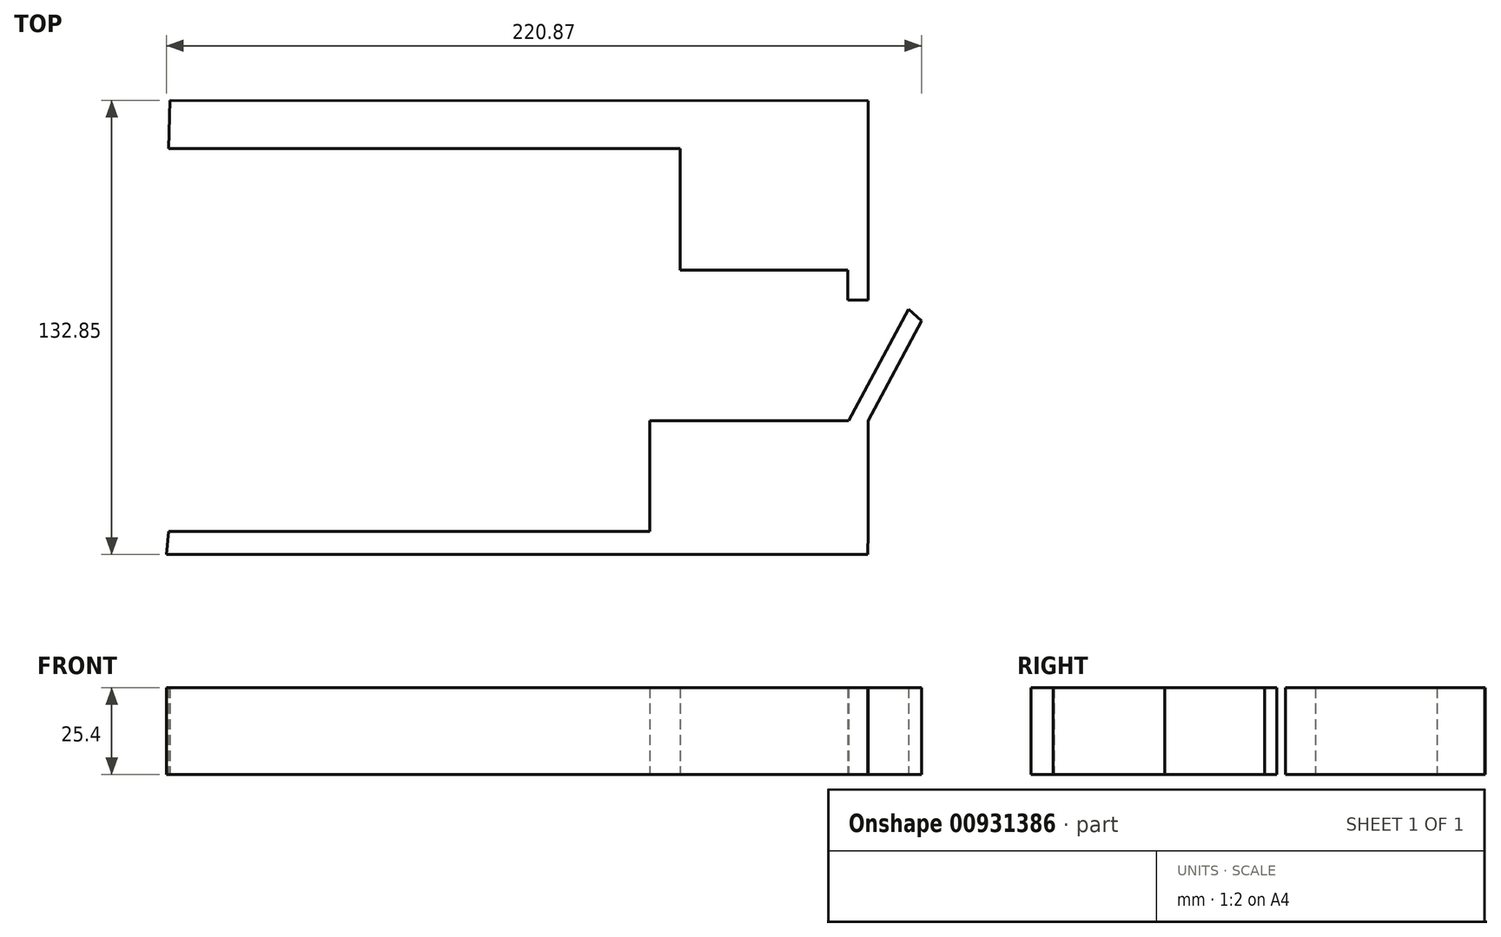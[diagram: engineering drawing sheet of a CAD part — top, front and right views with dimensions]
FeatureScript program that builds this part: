
annotation { "Feature Type Name" : "Feature", "Feature Type Description" : "" }
export const myFeature = defineFeature(function(context is Context, id is Id, definition is map)
    precondition{}
    {
        {
            var Q0;
            Q0=qCreatedBy(makeId("Top.planeOp"),FACE);
            var sketch = newSketch(context, id + "F0", { "sketchPlane" : qUnion([Q0])});
            skLineSegment(sketch, "E0", {"start": v(76.23, 56.13) * mm, "end": v(76.23, 11.87) * mm});
            skLineSegment(sketch, "E1", {"start": v(76.52, -55.86) * mm, "end": v(76.52, -23.48) * mm});
            skLineSegment(sketch, "E2", {"start": v(76.52, -23.48) * mm, "end": v(82.18, -23.48) * mm});
            skLineSegment(sketch, "E3", {"start": v(82.18, -23.48) * mm, "end": v(82.18, -56.13) * mm});
            skLineSegment(sketch, "E4", {"start": v(76.52, -55.86) * mm, "end": v(82.18, -56.13) * mm});
            skLineSegment(sketch, "E5", {"start": v(76.23, 11.87) * mm, "end": v(82.18, 11.87) * mm});
            skLineSegment(sketch, "E6", {"start": v(76.23, 56.13) * mm, "end": v(82.22, 56.13) * mm});
            skLineSegment(sketch, "E7", {"start": v(82.22, 56.13) * mm, "end": v(82.18, 11.87) * mm});
            skPoint(sketch, "E8.start.orphan", {"position": v(55.74, 0) * mm});
            skLineSegment(sketch, "E9", {"start": v(82.18, -23.48) * mm, "end": v(97.87, 5.76) * mm});
            skLineSegment(sketch, "E10", {"start": v(76.52, -23.48) * mm, "end": v(94.06, 9.22) * mm});
            skLineSegment(sketch, "E11", {"start": v(94.06, 9.22) * mm, "end": v(97.87, 5.76) * mm});
            skLineSegment(sketch, "E12", {"start": v(76.23, 56.13) * mm, "end": v(-122.33, 56.13) * mm});
            skLineSegment(sketch, "E13", {"start": v(76.52, -55.86) * mm, "end": v(-122.33, -55.86) * mm});
            skLineSegment(sketch, "E14", {"start": v(-122.33, 56.13) * mm, "end": v(-122.33, -55.86) * mm});
            skLineSegment(sketch, "E15", {"start": v(27.27, 11.87) * mm, "end": v(27.27, 56.13) * mm});
            skLineSegment(sketch, "E16", {"start": v(27.27, -38.5) * mm, "end": v(27.27, -55.86) * mm});
            skLineSegment(sketch, "E17", {"start": v(27.27, 20.64) * mm, "end": v(76.23, 20.64) * mm});
            skLineSegment(sketch, "E18", {"start": v(27.27, 50.41) * mm, "end": v(76.23, 50.41) * mm});
            skLineSegment(sketch, "E19", {"start": v(27.27, -23.48) * mm, "end": v(76.52, -23.48) * mm});
            skLineSegment(sketch, "E20", {"start": v(27.27, -23.48) * mm, "end": v(27.27, -55.86) * mm});
            skPoint(sketch, "E21.start.orphan", {"position": v(-26.78, -55.86) * mm});
            skLineSegment(sketch, "E22", {"start": v(82.18, -56.13) * mm, "end": v(82.08, -62.6) * mm});
            skLineSegment(sketch, "E23", {"start": v(82.08, -62.6) * mm, "end": v(-123, -62.6) * mm});
            skLineSegment(sketch, "E24", {"start": v(-123, -62.6) * mm, "end": v(-122.33, -55.86) * mm});
            skPoint(sketch, "E25.start.orphan", {"position": v(-26.78, 11.87) * mm});
            skLineSegment(sketch, "E26", {"start": v(27.24, 11.83) * mm, "end": v(18.33, 11.83) * mm});
            skLineSegment(sketch, "E27", {"start": v(18.33, 11.83) * mm, "end": v(18.33, 56.13) * mm});
            skLineSegment(sketch, "E28", {"start": v(27.27, -23.48) * mm, "end": v(18.33, -23.48) * mm});
            skLineSegment(sketch, "E29", {"start": v(18.33, -23.48) * mm, "end": v(18.33, -55.86) * mm});
            skLineSegment(sketch, "E30", {"start": v(82.22, 56.13) * mm, "end": v(82.22, 70.08) * mm});
            skLineSegment(sketch, "E31", {"start": v(82.22, 70.08) * mm, "end": v(-121.98, 70.25) * mm});
            skLineSegment(sketch, "E32", {"start": v(-121.98, 70.25) * mm, "end": v(-122.33, 56.13) * mm});
            skLineSegment(sketch, "E33", {"start": v(-37.58, 113.2) * mm, "end": v(-44, 131.35) * mm});
            skSolve(sketch);
        }
        {
            var Q0;
            Q0 = qSketchRegion(id + "F0", true);
            extrude(context, id + "F1", {"entities" : qUnion([Q0]), "depth" : 25.4 * mm, "offsetDistance" : 25.4 * mm});
        }
    });
